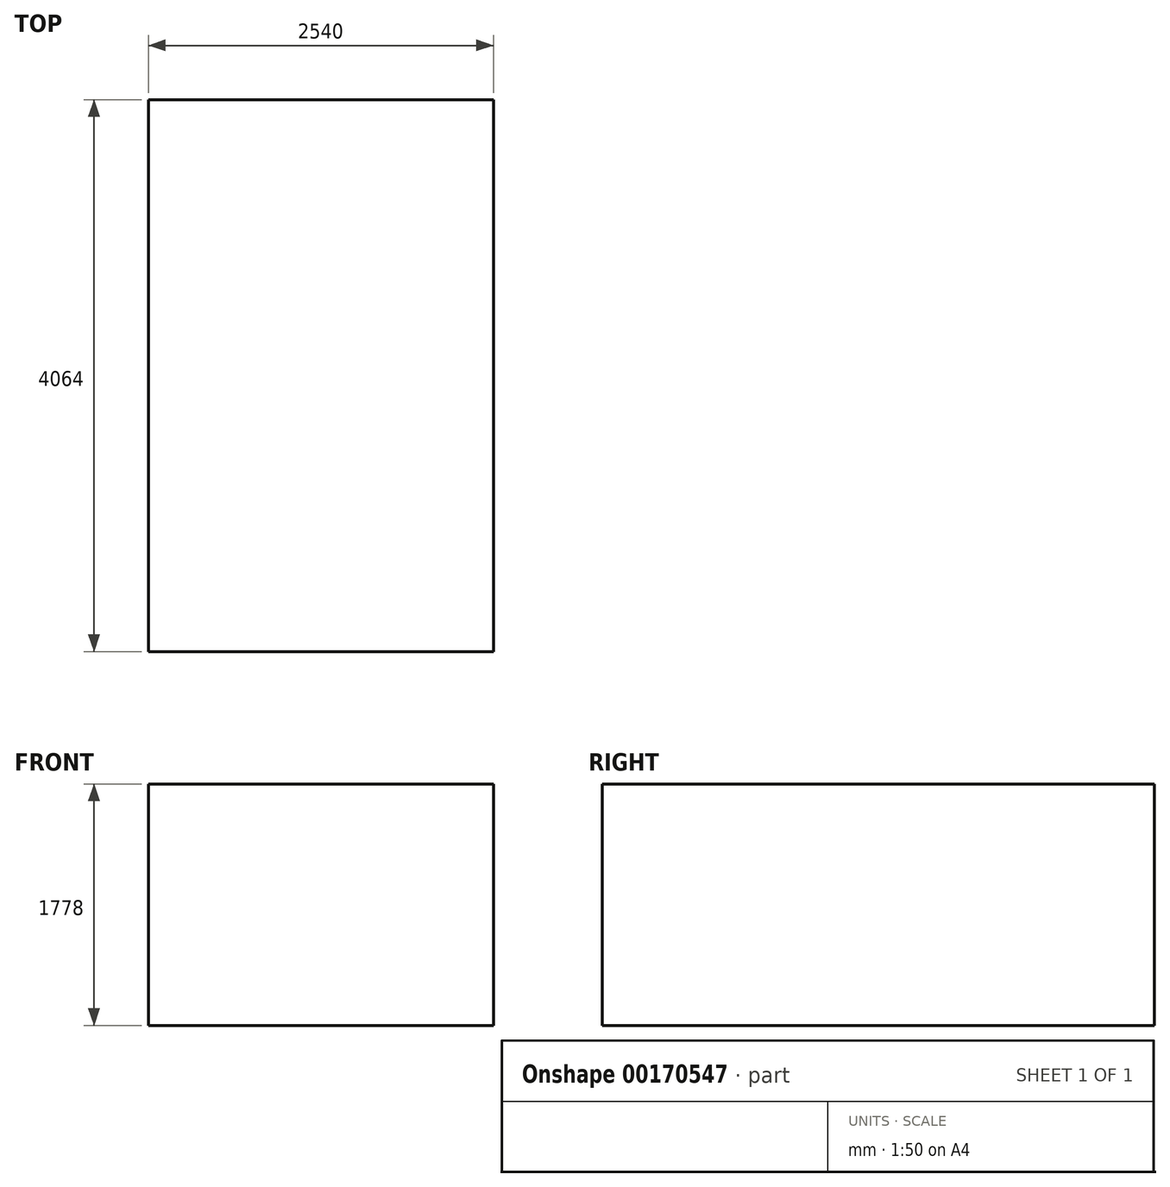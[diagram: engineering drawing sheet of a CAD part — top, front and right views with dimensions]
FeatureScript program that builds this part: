
annotation { "Feature Type Name" : "Feature", "Feature Type Description" : "" }
export const myFeature = defineFeature(function(context is Context, id is Id, definition is map)
    precondition{}
    {
        {
            var Q0;
            Q0=qCreatedBy(makeId("Top.planeOp"),FACE);
            var sketch = newSketch(context, id + "F0", { "sketchPlane" : qUnion([Q0])});
            skLineSegment(sketch, "E0.bottom", {"start": v(0, 0) * mm, "end": v(2540, 0) * mm});
            skLineSegment(sketch, "E0.top", {"start": v(0, 4064) * mm, "end": v(2540, 4064) * mm});
            skLineSegment(sketch, "E0.left", {"start": v(0, 0) * mm, "end": v(0, 4064) * mm});
            skLineSegment(sketch, "E0.right", {"start": v(2540, 0) * mm, "end": v(2540, 4064) * mm});
            skSolve(sketch);
        }
        {
            var Q0;
            Q0=makeQuery(id+"F0.imprint","IMPRINT",FACE,{"disambiguationData":[TD([[makeQuery(id+"F0.imprint","IMPRINT",EDGE,{"derivedFrom":sQuery(id+"F0.wireOp",EDGE,"E0.bottom")}),1.0]])]});
            extrude(context, id + "F1", {"entities" : qUnion([Q0]), "depth" : 1778 * mm});
        }
    });
